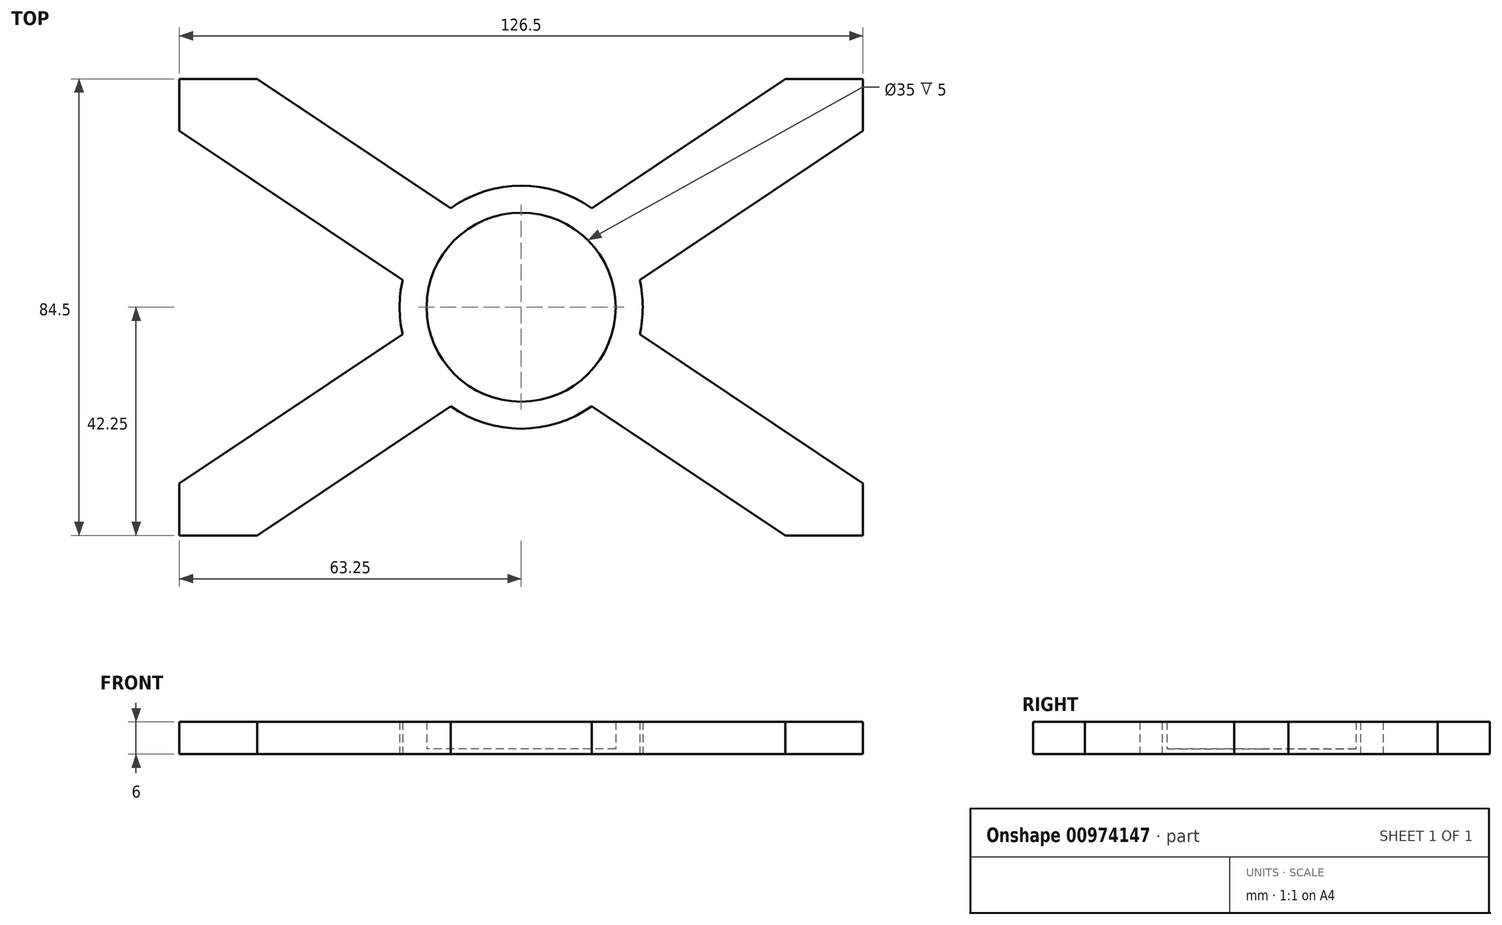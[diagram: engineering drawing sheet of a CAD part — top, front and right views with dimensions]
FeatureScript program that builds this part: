
annotation { "Feature Type Name" : "Feature", "Feature Type Description" : "" }
export const myFeature = defineFeature(function(context is Context, id is Id, definition is map)
    precondition{}
    {
        {
            var Q0;
            Q0=qCreatedBy(makeId("Top.planeOp"),FACE);
            var sketch = newSketch(context, id + "F0", { "sketchPlane" : qUnion([Q0])});
            skLineSegment(sketch, "E0.bottom", {"start": v(-63.25, -42.25) * mm, "end": v(63.25, -42.25) * mm});
            skLineSegment(sketch, "E0.top", {"start": v(-63.25, 42.25) * mm, "end": v(63.25, 42.25) * mm});
            skLineSegment(sketch, "E0.left", {"start": v(-63.25, -42.25) * mm, "end": v(-63.25, 42.25) * mm});
            skLineSegment(sketch, "E0.right", {"start": v(63.25, -42.25) * mm, "end": v(63.25, 42.25) * mm});
            skPoint(sketch, "E0.middle", {"position": v(0, 0) * mm});
            skCircle(sketch, "E1", {"center": v(0, 0) * mm, "radius": 17.5 * mm});
            skLineSegment(sketch, "E2.0", {"start": v(48.85, 42.25) * mm, "end": v(13.04, 18.33) * mm});
            skLineSegment(sketch, "E3.0", {"start": v(63.25, 32.63) * mm, "end": v(21.93, 5.03) * mm});
            skLineSegment(sketch, "E4.0", {"start": v(-63.25, 32.63) * mm, "end": v(-21.93, 5.03) * mm});
            skLineSegment(sketch, "E5.0", {"start": v(-48.85, 42.25) * mm, "end": v(-13.04, 18.33) * mm});
            skLineSegment(sketch, "E6.trimOffspring", {"start": v(-21.93, -5.03) * mm, "end": v(-63.25, -32.63) * mm});
            skLineSegment(sketch, "E7.trimOffspring", {"start": v(-13.04, -18.33) * mm, "end": v(-48.85, -42.25) * mm});
            skLineSegment(sketch, "E8.trimOffspring", {"start": v(21.93, -5.03) * mm, "end": v(63.25, -32.63) * mm});
            skLineSegment(sketch, "E9.trimOffspring", {"start": v(13.04, -18.33) * mm, "end": v(48.85, -42.25) * mm});
            skArc(sketch, "E10", {"start": v(-21.93, 5.03) * mm, "mid": v(-22.5, 0) * mm, "end": v(-21.93, -5.03) * mm});
            skArc(sketch, "E11.trimOffspring", {"start": v(-13.04, -18.33) * mm, "mid": v(0, -22.5) * mm, "end": v(13.04, -18.33) * mm});
            skArc(sketch, "E12.trimOffspring", {"start": v(21.93, -5.03) * mm, "mid": v(22.5, 0) * mm, "end": v(21.93, 5.03) * mm});
            skArc(sketch, "E13.trimOffspring", {"start": v(13.04, 18.33) * mm, "mid": v(0, 22.5) * mm, "end": v(-13.04, 18.33) * mm});
            skSolve(sketch);
        }
        {
            var Q0;
            Q0=makeQuery(id+"F0.imprint","IMPRINT",FACE,{"disambiguationData":[TD([[makeQuery(id+"F0.imprint","IMPRINT",EDGE,{"derivedFrom":sQuery(id+"F0.wireOp",EDGE,"E1")}),-1.0]])]});
            extrude(context, id + "F1", {"entities" : qUnion([Q0]), "depth" : 6 * mm, "offsetDistance" : 25 * mm});
        }
        {
            var Q0;
            Q0=makeQuery(id+"F0.imprint","IMPRINT",FACE,{"disambiguationData":[TD([[makeQuery(id+"F0.imprint","IMPRINT",EDGE,{"derivedFrom":sQuery(id+"F0.wireOp",EDGE,"E1")}),1.0]])]});
            extrude(context, id + "F2", {"entities" : qUnion([Q0]), "operationType" : NewBodyOperationType.ADD, "depth" : 1 * mm, "offsetDistance" : 25 * mm});
        }
    });
